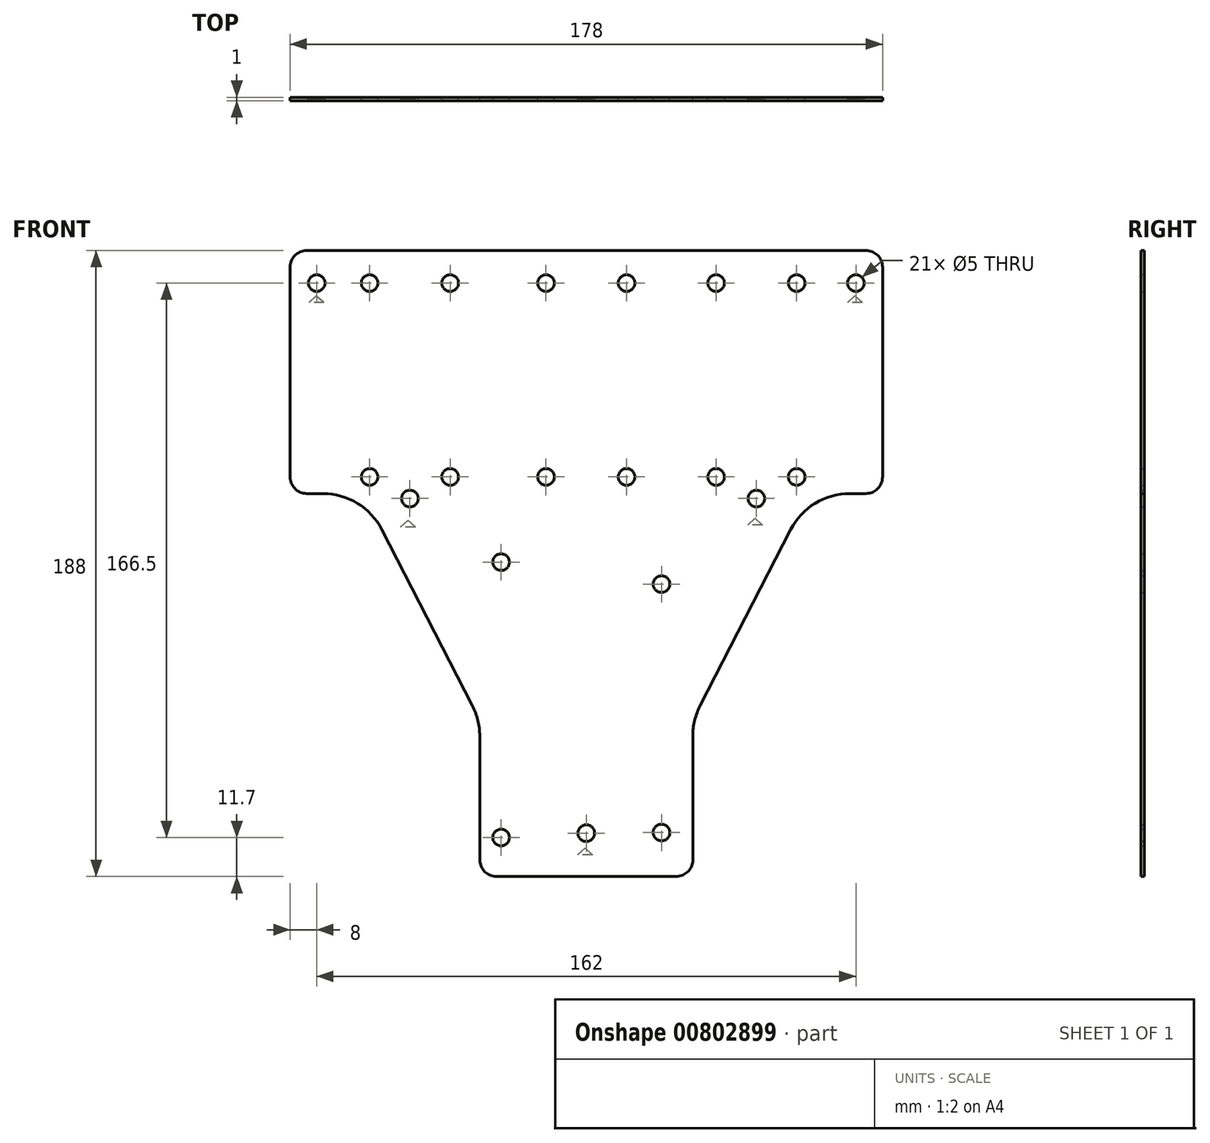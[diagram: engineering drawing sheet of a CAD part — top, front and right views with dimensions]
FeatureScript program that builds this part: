
annotation { "Feature Type Name" : "Feature", "Feature Type Description" : "" }
export const myFeature = defineFeature(function(context is Context, id is Id, definition is map)
    precondition{}
    {
        {
            var Q0;
            Q0=qCreatedBy(makeId("Front.planeOp"),FACE);
            var sketch = newSketch(context, id + "F0", { "sketchPlane" : qUnion([Q0])});
            skLineSegment(sketch, "E0.bottom", {"start": v(89, 83) * mm, "end": v(-89, 83) * mm});
            skLineSegment(sketch, "E0.top", {"start": v(89, -105) * mm, "end": v(-89, -105) * mm});
            skLineSegment(sketch, "E0.left", {"start": v(89, 83) * mm, "end": v(89, -105) * mm});
            skLineSegment(sketch, "E0.right", {"start": v(-89, 83) * mm, "end": v(-89, -105) * mm});
            skSolve(sketch);
        }
        {
            var Q0;
            Q0=qSketchRegion(id+"F0",true);
            extrude(context, id + "F1", {"entities" : qUnion([Q0]), "depth" : 1 * mm, "offsetDistance" : 25 * mm});
        }
        {
            var Q0;
            Q0=makeQuery(id+"F1.opExtrude","CAP_FACE",FACE,{"disambiguationData":[OSD([sQuery(id+"F0.wireOp",EDGE,"E0.bottom"),sQuery(id+"F0.wireOp",EDGE,"E0.top"),sQuery(id+"F0.wireOp",EDGE,"E0.left"),sQuery(id+"F0.wireOp",EDGE,"E0.right")])],"isStart":true});
            var sketch = newSketch(context, id + "F2", { "sketchPlane" : qUnion([Q0])});
            skCircle(sketch, "E1", {"center": v(-81, 73.2) * mm, "radius": 2.5 * mm});
            skCircle(sketch, "E2", {"center": v(81, 73.2) * mm, "radius": 2.5 * mm});
            skCircle(sketch, "E3", {"center": v(53, 8.5) * mm, "radius": 2.5 * mm});
            skCircle(sketch, "E4", {"center": v(-51.1, 8.5) * mm, "radius": 2.5 * mm});
            skCircle(sketch, "E5", {"center": v(0, -92) * mm, "radius": 2.5 * mm});
            skCircle(sketch, "E6", {"center": v(-22.6, -91.8) * mm, "radius": 2.5 * mm});
            skCircle(sketch, "E7", {"center": v(25.6, -93.3) * mm, "radius": 2.5 * mm});
            skCircle(sketch, "E8", {"center": v(-22.6, -17.2) * mm, "radius": 2.5 * mm});
            skCircle(sketch, "E9", {"center": v(25.6, -10.6) * mm, "radius": 2.5 * mm});
            skCircle(sketch, "E10", {"center": v(-63.2, 73.2) * mm, "radius": 2.5 * mm});
            skCircle(sketch, "E11", {"center": v(-39, 73.2) * mm, "radius": 2.5 * mm});
            skCircle(sketch, "E12", {"center": v(-39, 15) * mm, "radius": 2.5 * mm});
            skCircle(sketch, "E13", {"center": v(-63.2, 15) * mm, "radius": 2.5 * mm});
            skCircle(sketch, "E14", {"center": v(40.9, 73.2) * mm, "radius": 2.5 * mm});
            skCircle(sketch, "E15", {"center": v(65.1, 73.2) * mm, "radius": 2.5 * mm});
            skCircle(sketch, "E16", {"center": v(65.1, 15) * mm, "radius": 2.5 * mm});
            skCircle(sketch, "E17", {"center": v(40.9, 15) * mm, "radius": 2.5 * mm});
            skCircle(sketch, "E18", {"center": v(-12.1, 73.2) * mm, "radius": 2.5 * mm});
            skCircle(sketch, "E19", {"center": v(12.1, 73.2) * mm, "radius": 2.5 * mm});
            skCircle(sketch, "E20", {"center": v(-12.1, 15) * mm, "radius": 2.5 * mm});
            skCircle(sketch, "E21", {"center": v(12.1, 15) * mm, "radius": 2.5 * mm});
            skSolve(sketch);
        }
        {
            var Q0;
            Q0=qSketchRegion(id+"F2",true);
            extrude(context, id + "F3", {"entities" : qUnion([Q0]), "operationType" : NewBodyOperationType.REMOVE, "endBound" : BoundingType.THROUGH_ALL, "oppositeDirection" : true, "depth" : 25 * mm, "offsetDistance" : 25 * mm});
        }
        {
            var Q0;
            Q0=makeQuery(id+"F2.imprint","IMPRINT",FACE,{"disambiguationData":[TD([[makeQuery(id+"F2.imprint","IMPRINT",EDGE,{"derivedFrom":sQuery(id+"F2.wireOp",EDGE,"E1")}),-1.0]])]});
            var sketch = newSketch(context, id + "F4", { "sketchPlane" : qUnion([Q0])});
            skLineSegment(sketch, "E22", {"start": v(-32, -113) * mm, "end": v(-94, -113) * mm});
            skLineSegment(sketch, "E23", {"start": v(-94, -113) * mm, "end": v(-94, 10) * mm});
            skLineSegment(sketch, "E24", {"start": v(32, -113) * mm, "end": v(94, -113) * mm});
            skLineSegment(sketch, "E25", {"start": v(94, -113) * mm, "end": v(94, 10) * mm});
            skLineSegment(sketch, "E26", {"start": v(32, -58) * mm, "end": v(32, -113) * mm});
            skLineSegment(sketch, "E27", {"start": v(-32, -58) * mm, "end": v(-32, -113) * mm});
            skLineSegment(sketch, "E28", {"start": v(94, 10) * mm, "end": v(67, 10) * mm});
            skLineSegment(sketch, "E29", {"start": v(67, 10) * mm, "end": v(32, -58) * mm});
            skLineSegment(sketch, "E30", {"start": v(-94, 10) * mm, "end": v(-67, 10) * mm});
            skLineSegment(sketch, "E31", {"start": v(-67, 10) * mm, "end": v(-32, -58) * mm});
            skSolve(sketch);
        }
        {
            var Q0;
            Q0=qSketchRegion(id+"F4",true);
            extrude(context, id + "F5", {"entities" : qUnion([Q0]), "operationType" : NewBodyOperationType.REMOVE, "endBound" : BoundingType.THROUGH_ALL, "oppositeDirection" : true, "depth" : 25 * mm, "offsetDistance" : 25 * mm});
        }
        {
            var Q0;
            Q0=makeQuery(id+"F1.opExtrude","SWEPT_EDGE",EDGE,{"disambiguationData":[OSD([sQuery(id+"F0.wireOp",EDGE,"E0.bottom"),sQuery(id+"F0.wireOp",EDGE,"E0.left")])]});
            var Q1;
            Q1=makeQuery(id+"F1.opExtrude","SWEPT_EDGE",EDGE,{"disambiguationData":[OSD([sQuery(id+"F0.wireOp",EDGE,"E0.bottom"),sQuery(id+"F0.wireOp",EDGE,"E0.right")])]});
            var Q2;
            Q2=makeQuery(id+"F5.boolean.opBoolean","INTERSECT",EDGE,{"derivedFrom":[makeQuery(id+"F1.opExtrude","SWEPT_FACE",FACE,{"disambiguationData":[OSD([sQuery(id+"F0.wireOp",EDGE,"E0.right")])]}),makeQuery(id+"F5.opExtrude","SWEPT_FACE",FACE,{"disambiguationData":[OSD([sQuery(id+"F4.wireOp",EDGE,"E28")])]})]});
            var Q3;
            Q3=makeQuery(id+"F5.boolean.opBoolean","INTERSECT",EDGE,{"derivedFrom":[makeQuery(id+"F1.opExtrude","SWEPT_FACE",FACE,{"disambiguationData":[OSD([sQuery(id+"F0.wireOp",EDGE,"E0.top")])]}),makeQuery(id+"F5.opExtrude","SWEPT_FACE",FACE,{"disambiguationData":[OSD([sQuery(id+"F4.wireOp",EDGE,"E26")])]})]});
            var Q4;
            Q4=makeQuery(id+"F5.boolean.opBoolean","INTERSECT",EDGE,{"derivedFrom":[makeQuery(id+"F1.opExtrude","SWEPT_FACE",FACE,{"disambiguationData":[OSD([sQuery(id+"F0.wireOp",EDGE,"E0.top")])]}),makeQuery(id+"F5.opExtrude","SWEPT_FACE",FACE,{"disambiguationData":[OSD([sQuery(id+"F4.wireOp",EDGE,"E27")])]})]});
            var Q5;
            Q5=makeQuery(id+"F5.boolean.opBoolean","INTERSECT",EDGE,{"derivedFrom":[makeQuery(id+"F1.opExtrude","SWEPT_FACE",FACE,{"disambiguationData":[OSD([sQuery(id+"F0.wireOp",EDGE,"E0.left")])]}),makeQuery(id+"F5.opExtrude","SWEPT_FACE",FACE,{"disambiguationData":[OSD([sQuery(id+"F4.wireOp",EDGE,"E30")])]})]});
            fillet(context, id + "F6", {"entities" : qUnion([Q0, Q1, Q2, Q3, Q4, Q5]), "radius" : 5 * mm, "tangentPropagation" : true, "allowEdgeOverflow" : false});
        }
        {
            var Q0;
            Q0=makeQuery(id+"F5.boolean.opBoolean","COPY",EDGE,{"derivedFrom":makeQuery(id+"F5.opExtrude","SWEPT_EDGE",EDGE,{"disambiguationData":[OSD([sQuery(id+"F4.wireOp",EDGE,"E30"),sQuery(id+"F4.wireOp",EDGE,"E31")])]})});
            var Q1;
            Q1=makeQuery(id+"F5.boolean.opBoolean","COPY",EDGE,{"derivedFrom":makeQuery(id+"F5.opExtrude","SWEPT_EDGE",EDGE,{"disambiguationData":[OSD([sQuery(id+"F4.wireOp",EDGE,"E27"),sQuery(id+"F4.wireOp",EDGE,"E31")])]})});
            var Q2;
            Q2=makeQuery(id+"F5.boolean.opBoolean","COPY",EDGE,{"derivedFrom":makeQuery(id+"F5.opExtrude","SWEPT_EDGE",EDGE,{"disambiguationData":[OSD([sQuery(id+"F4.wireOp",EDGE,"E26"),sQuery(id+"F4.wireOp",EDGE,"E29")])]})});
            var Q3;
            Q3=makeQuery(id+"F5.boolean.opBoolean","COPY",EDGE,{"derivedFrom":makeQuery(id+"F5.opExtrude","SWEPT_EDGE",EDGE,{"disambiguationData":[OSD([sQuery(id+"F4.wireOp",EDGE,"E28"),sQuery(id+"F4.wireOp",EDGE,"E29")])]})});
            fillet(context, id + "F7", {"entities" : qUnion([Q0, Q1, Q2, Q3]), "radius" : 20 * mm, "tangentPropagation" : true, "allowEdgeOverflow" : false});
        }
        {
            var Q0;
            Q0=makeQuery(id+"F0.imprint","IMPRINT",FACE,{"disambiguationData":[TD([[makeQuery(id+"F0.imprint","IMPRINT",EDGE,{"derivedFrom":sQuery(id+"F0.wireOp",EDGE,"E0.bottom")}),1.0]])]});
            var sketch = newSketch(context, id + "F8", { "sketchPlane" : qUnion([Q0])});
            skLineSegment(sketch, "E32", {"start": v(80.66, 69.43) * mm, "end": v(82.95, 67.37) * mm});
            skLineSegment(sketch, "E33", {"start": v(82.95, 67.37) * mm, "end": v(78.45, 67.37) * mm});
            skLineSegment(sketch, "E34", {"start": v(78.45, 67.37) * mm, "end": v(80.66, 69.43) * mm});
            skLineSegment(sketch, "E35", {"start": v(50.69, 2.6) * mm, "end": v(52.97, 0.53) * mm});
            skLineSegment(sketch, "E36", {"start": v(52.97, 0.53) * mm, "end": v(48.48, 0.53) * mm});
            skLineSegment(sketch, "E37", {"start": v(48.48, 0.53) * mm, "end": v(50.69, 2.6) * mm});
            skLineSegment(sketch, "E38", {"start": v(-53.59, 2) * mm, "end": v(-51.3, -0.06) * mm});
            skLineSegment(sketch, "E39", {"start": v(-51.3, -0.06) * mm, "end": v(-55.8, -0.06) * mm});
            skLineSegment(sketch, "E40", {"start": v(-55.8, -0.06) * mm, "end": v(-53.59, 2) * mm});
            skLineSegment(sketch, "E41", {"start": v(-0.4, -96.45) * mm, "end": v(1.9, -98.52) * mm});
            skLineSegment(sketch, "E42", {"start": v(1.9, -98.52) * mm, "end": v(-2.6, -98.52) * mm});
            skLineSegment(sketch, "E43", {"start": v(-2.6, -98.52) * mm, "end": v(-0.4, -96.45) * mm});
            skLineSegment(sketch, "E44", {"start": v(-81.09, 69.44) * mm, "end": v(-78.8, 67.37) * mm});
            skLineSegment(sketch, "E45", {"start": v(-78.8, 67.37) * mm, "end": v(-83.3, 67.37) * mm});
            skLineSegment(sketch, "E46", {"start": v(-83.3, 67.37) * mm, "end": v(-81.09, 69.44) * mm});
            skSolve(sketch);
        }
        {
            var Q0;
            Q0=qSketchRegion(id+"F8",true);
            extrude(context, id + "F9", {"entities" : qUnion([Q0]), "operationType" : NewBodyOperationType.REMOVE, "depth" : 0.3 * mm, "offsetDistance" : 25 * mm});
        }
    });
